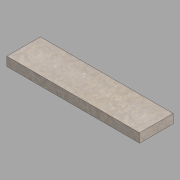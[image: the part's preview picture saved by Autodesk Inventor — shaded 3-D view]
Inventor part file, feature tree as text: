
AUTODESK INVENTOR PART (.ipt)
format: ipt  version: 2022.2 (Build 262287000, 287)  size: 104,960 bytes
history: native  units: in
note: dims shown in document units (in); Inventor stores cm internally (conversion verified against a paired STEP export)
features: extrude x1, sketch x1
ambient origin geometry x8: Origin, YZ Plane, XZ Plane, XY Plane, X Axis, Y Axis, Z Axis, Center Point
bodies: Solid1 (feature_tree)
feature tree (2):
  extrude  "Extrusion1"  Depth=15.0in
  sketch  "Sketch1"  dims[d0=4.0in d1=15.0in d2=59.375in d3=0.0in]
